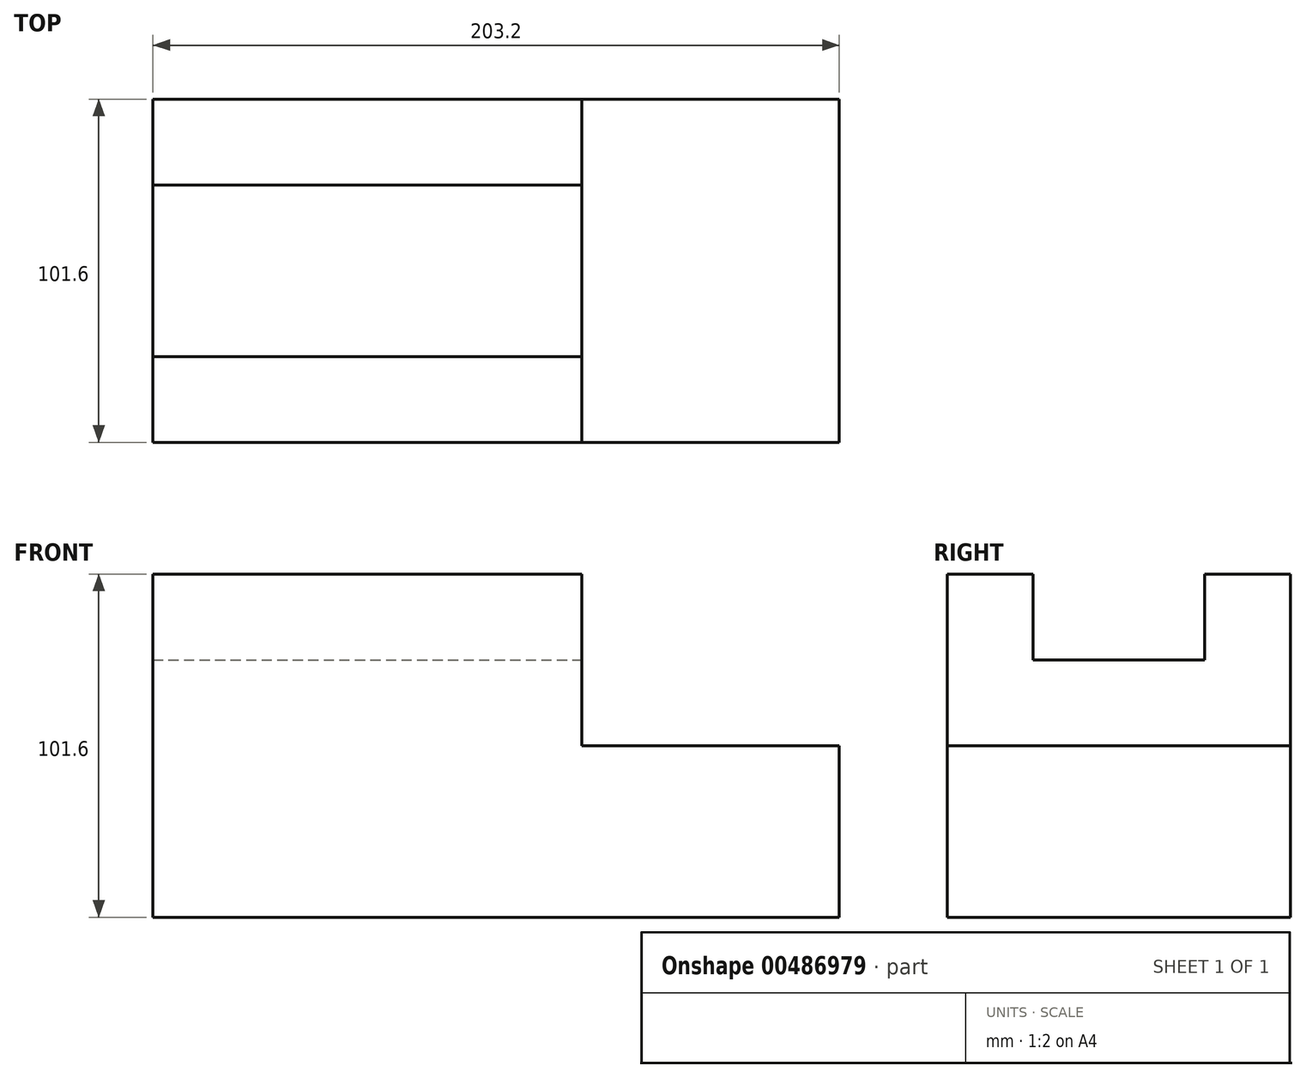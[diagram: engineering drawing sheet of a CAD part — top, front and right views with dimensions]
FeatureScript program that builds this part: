
annotation { "Feature Type Name" : "Feature", "Feature Type Description" : "" }
export const myFeature = defineFeature(function(context is Context, id is Id, definition is map)
    precondition{}
    {
        {
            var Q0;
            Q0=qCreatedBy(makeId("Top.planeOp"),FACE);
            var sketch = newSketch(context, id + "F0", { "sketchPlane" : qUnion([Q0])});
            skLineSegment(sketch, "E0.bottom", {"start": v(-42.86, -22.32) * mm, "end": v(160.34, -22.32) * mm});
            skLineSegment(sketch, "E0.top", {"start": v(-42.86, 28.48) * mm, "end": v(160.34, 28.48) * mm});
            skLineSegment(sketch, "E0.left", {"start": v(-42.86, -22.32) * mm, "end": v(-42.86, 28.48) * mm});
            skLineSegment(sketch, "E0.right", {"start": v(160.34, -22.32) * mm, "end": v(160.34, 28.48) * mm});
            skSolve(sketch);
        }
        {
            var Q0;
            Q0 = qSketchRegion(id + "F0", true);
            extrude(context, id + "F1", {"entities" : qUnion([Q0]), "depth" : 101.6 * mm});
        }
        {
            var Q0;
            Q0=qCreatedBy(makeId("Top.planeOp"),FACE);
            var sketch = newSketch(context, id + "F2", { "sketchPlane" : qUnion([Q0])});
            skLineSegment(sketch, "E1.bottom", {"start": v(-42.86, 28.48) * mm, "end": v(84.14, 28.48) * mm});
            skLineSegment(sketch, "E1.top", {"start": v(-42.86, 53.88) * mm, "end": v(84.14, 53.88) * mm});
            skLineSegment(sketch, "E1.left", {"start": v(-42.86, 28.48) * mm, "end": v(-42.86, 53.88) * mm});
            skLineSegment(sketch, "E1.right", {"start": v(84.14, 28.48) * mm, "end": v(84.14, 53.88) * mm});
            skSolve(sketch);
        }
        {
            var Q0;
            Q0 = qSketchRegion(id + "F2", true);
            extrude(context, id + "F3", {"entities" : qUnion([Q0]), "operationType" : NewBodyOperationType.ADD, "depth" : 101.6 * mm});
        }
        {
            var Q0;
            Q0=qCreatedBy(makeId("Top.planeOp"),FACE);
            var sketch = newSketch(context, id + "F4", { "sketchPlane" : qUnion([Q0])});
            skLineSegment(sketch, "E2.bottom", {"start": v(-42.86, 53.88) * mm, "end": v(84.14, 53.88) * mm});
            skLineSegment(sketch, "E2.top", {"start": v(-42.86, 79.28) * mm, "end": v(84.14, 79.28) * mm});
            skLineSegment(sketch, "E2.left", {"start": v(-42.86, 53.88) * mm, "end": v(-42.86, 79.28) * mm});
            skLineSegment(sketch, "E2.right", {"start": v(84.14, 53.88) * mm, "end": v(84.14, 79.28) * mm});
            skSolve(sketch);
        }
        {
            var Q0;
            Q0 = qSketchRegion(id + "F4", true);
            extrude(context, id + "F5", {"entities" : qUnion([Q0]), "operationType" : NewBodyOperationType.ADD, "depth" : 25.4 * mm});
        }
        {
            var Q0;
            Q0=makeQuery(id+"F3.boolean.opBoolean","MERGE",FACE,{"derivedFrom":[makeQuery(id+"F1.opExtrude","CAP_FACE",FACE,{"disambiguationData":[OSD([sQuery(id+"F0.wireOp",EDGE,"E0.bottom"),sQuery(id+"F0.wireOp",EDGE,"E0.top"),sQuery(id+"F0.wireOp",EDGE,"E0.left"),sQuery(id+"F0.wireOp",EDGE,"E0.right")])],"isStart":false}),makeQuery(id+"F3.opExtrude","CAP_FACE",FACE,{"disambiguationData":[OSD([sQuery(id+"F2.wireOp",EDGE,"E1.bottom"),sQuery(id+"F2.wireOp",EDGE,"E1.top"),sQuery(id+"F2.wireOp",EDGE,"E1.left"),sQuery(id+"F2.wireOp",EDGE,"E1.right")])],"isStart":false})]});
            var sketch = newSketch(context, id + "F6", { "sketchPlane" : qUnion([Q0])});
            skLineSegment(sketch, "E3.bottom", {"start": v(-42.86, 53.88) * mm, "end": v(84.14, 53.88) * mm});
            skLineSegment(sketch, "E3.top", {"start": v(-42.86, 79.28) * mm, "end": v(84.14, 79.28) * mm});
            skLineSegment(sketch, "E3.left", {"start": v(-42.86, 53.88) * mm, "end": v(-42.86, 79.28) * mm});
            skLineSegment(sketch, "E3.right", {"start": v(84.14, 53.88) * mm, "end": v(84.14, 79.28) * mm});
            skSolve(sketch);
        }
        {
            var Q0;
            Q0 = qSketchRegion(id + "F6", true);
            extrude(context, id + "F7", {"entities" : qUnion([Q0]), "operationType" : NewBodyOperationType.ADD, "oppositeDirection" : true, "depth" : 25.4 * mm});
        }
        {
            var Q0;
            Q0=makeQuery(id+"F1.opExtrude","SWEPT_BODY",BODY,{"disambiguationData":[OSD([sQuery(id+"F0.wireOp",EDGE,"E0.bottom"),sQuery(id+"F0.wireOp",EDGE,"E0.top"),sQuery(id+"F0.wireOp",EDGE,"E0.left"),sQuery(id+"F0.wireOp",EDGE,"E0.right")])]});
            var Q1;
            Q1=makeQuery(id+"F1.opExtrude","CAP_EDGE",EDGE,{"disambiguationData":[OSD([sQuery(id+"F0.wireOp",EDGE,"E0.bottom")])],"isStart":true});
            transform(context, id + "F8", {"entities" : qUnion([Q0]), "transformType" : TransformType.ROTATION, "transformAxis" : qUnion([Q1]), "angle" : 90 * degree, "makeCopy" : false});
        }
    });
